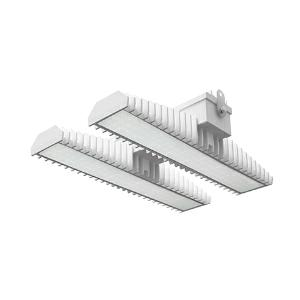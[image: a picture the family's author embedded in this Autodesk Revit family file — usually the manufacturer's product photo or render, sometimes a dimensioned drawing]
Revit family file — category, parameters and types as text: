
# Revit family: 3f_filippi_-_3f_lem_ht_concentrato_3f_filippi_-_59032_a0812_-_3f_lem_2_ht_led_60_cr_conc___vs_5d9f
name_source: partatom
category: Lighting Fixtures
units: mm (PartAtom-declared; Revit-internal decimal feet)

## family parameters
Cut with Voids When Loaded = No
Host = Face
Light Source = No
Part Type = Normal
Room Calculation Point = No
Round Connector Dimension = Use Diameter
Shared = No

## types (1)
- 3F Filippi - 3F LEM HT Concentrato (1 x LED, 8455 lm, 68 W, 4000 K)
    Apparent Load = 68 VA
    Approval mark = ENEC
    CIE Flux Codes = 78 93 98 100 100
    Color Rendering = 80
    Color Temperature = 4000 K
    Control Gear = Electronic ballast
    Default Elevation = 1800 mm
    Description = Industrial luminaire with high light output and high luminous efficiency designed with the most innovative technologies for environments with temperature up to 70°C.

ILLUMINOTECHNICAL
Luminous efficiency 100% (DLOR 98%, ULOR 2%).
Initial luminous flux of the luminaire 8455 lm.
Direct symmetric narrow distribution: the illuminated area has a elliptical shape.
Installation Interdistance Transv.D = 0.60 x hu - Long.D = 0.91 x hu.
Tabular UGR (CIE 117 - 4H-8H; S=0.25H; 70/50/20): RUG 17.9 - 19.5.
Beam angle: 38° - 61°.
Luminous efficacy 124 lm/W.
Lifetime (L93/B10): 30000 h. (tq+25°C)
Lifetime (L90/B10): 50000 h. (tq+25°C)
Lifetime (L85/B10): 80000 h. (tq+25°C)
Lifetime (L80/B10): 100000 h. (tq+25°C)
Lifetime (L85/B10): 50000 h. (tq+70°C)
Sudden decreased luminous flux after 50000 hours: 0% (C0).
Photobiological safety in compliance with IEC/TR 62778: RG0 risk exempt, (IEC 62471).
In compliance with IEC/EN 62722-2-1 - IEC/EN 62717 standards.
Luminous flux at +70°C: -13.5%.

SOURCE
2 Mid-Power linear LED modules 30W/840.
Energy efficiency class (UE 2019/2020 - UE 2019/2015): C.
CIE 13.3 Colour rendering index: CRI >80 (R9 <50%).
IES TM-30 Fidelity Index: Rf = 84 Rg = 95.
CCT nominal colour temperature 4000 K.
Colour initial tolerance (MacAdam): SDCM 3.

MECHANICAL
Passive modular heatsinks in die-casted aluminium, painted in white colour.
To optimize the thermal management of the LED module, the heatsinks are oversized and provided with self-cleaning of cooling fins.
Wiring body in aluminium and galvanised steel anchored solidly to the sinks and thermally separated.
3F Lens lenses with high luminous efficiency, transparent polycarbonate, fixed to the LED modules.
Fixing brackets in stainless steel.
Luminaire with limited surface temperature. - D - (EN 60598-2-24)
Dimensions: 470x542 mm, height 133 mm. Weight 10.235 kg.
IP65 protection degree.
Mechanical strength to impacts IK08 (5 joule).
Glow-wire test resistance 850°C.

ELECTRICAL
Halogen Free electronic wiring 230V-50/60Hz, power factor 0.95, THD <25%, constant output current, class I, 1 driver.
Power of the luminaire 68 W.
CE - IEC 60598-1 - EN 60598-1.
SAFE FLICKER: PstLM=<1 and SVM=<0.4 (IEC TR 61547-1 and IEC TR 63158), to ensure a more comfortable and safe light.
Luminaire compliant with EN 60598-2-22 for power supply from a centralised emergency system CPSS (Central Power Supply System), not incorporated in the luminaire - high risk areas excluded. The default power and flux are 100% in AC and 100% in DC.
Ambient temperature from -30°C to +70°C.
Temperature class T6 max 85°C.
Quick connection via M20 3P connector with 9-13 mm tightening range.
Power unit positioned on a separate compartment by the LED module to ensure optimum temperatures of cabling components, to be inspectable and maintainable.
Relative humidity UR: <85%.

INSTALLATION
Ceiling / Suspended / Wall.
All accessories dedicated to this product are available on the Catalog and on our website www.3F-Filippi.com.

ACCESSORIES
A0812 - Anti-glare microprismatic VS moulded glass, tempered, not flammable, with sealing gasket.
One required for each light module. The pack contains 10 pieces.

APPLICATIONS
In commercial environments, exhibition and industrial areas, stores, open areas.
Applications with high ambient temperature up to 70°C.

WARNING
Fixture not suitable for cold stores with an ambient temperature <0°C and/or relative humidity >85%.
Luminaire designed for disposal/recycling at end-of-life.
Replaceable (LED only) light source by a professional. Replaceable control gear by a professional.
    Height = 133 mm  [stored 0.436352 ft]
    Lamp = 1 x LED
    Lamp Light Flux = 8455 lm
    Lamp Power = 68 W
    Lamp count = 1
    Length = 470 mm
    Lifetime = 50000 h
    Luminous efficacy = 124 lm/W
    Manufacturer = 3F Filippi
    ModVariant = No
    Model = 3F Filippi - 59032+A0812 - 3F LEM 2 HT LED 60 CR CONC + VS
    Mounting Place = Ceiling
    Mounting Type = Pendant
    Number of Poles = 1
    OnlyDefault = Yes
    Power Factor = 1
    Product Name = 3F Filippi - 3F LEM HT Concentrato
    Product group = pendant luminaire
    ProductGroupID = 9
    Protection Class = Protection class I
    Protection Degree = IP 65
    RLX_Detail_Level = 1
    RLX_Emergency_Light_Flux = 0 lm
    RLX_Emergency_Type = 0
    RLX_Emergency_Type_DB = No
    RlxData = <blob elided: 94937 chars, md5=0a1b41b4>
    Socket = socket
    Standby Power = 0 W
    System Light Flux = 8455 lm
    System Power = 68 W
    Type Comments = Product without accessories
    Type Image = 3f_filippi_-_lem_2__a0812.jpg
    URL = http://relux.com
    VarID = ---
    Voltage = 0 V
    Weight = 0.00 kg
    Width = 542 mm

note: [stored X ft] marks values corroborated as IEEE doubles in the binary element streams (Revit-internal decimal feet)

## geometry (parser evidence)
native form markers: Blend x4, Sweep x11
no freeform markers — native parametric forms only
